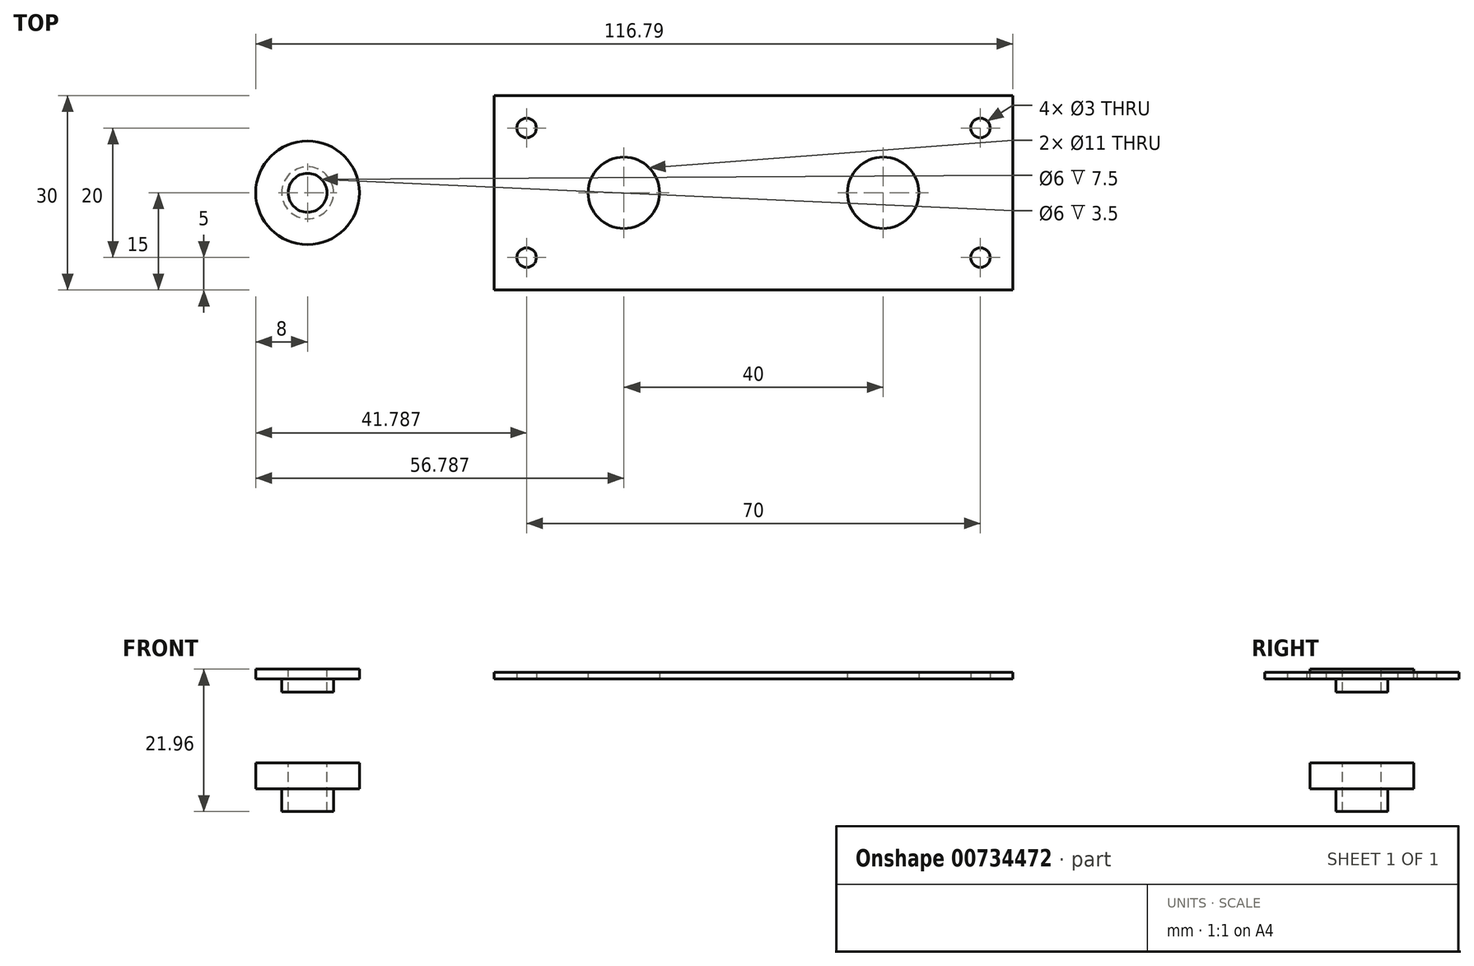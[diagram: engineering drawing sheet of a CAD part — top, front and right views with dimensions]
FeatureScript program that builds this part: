
annotation { "Feature Type Name" : "Feature", "Feature Type Description" : "" }
export const myFeature = defineFeature(function(context is Context, id is Id, definition is map)
    precondition{}
    {
        {
            var Q0;
            Q0=qCreatedBy(makeId("Front.planeOp"),FACE);
            var sketch = newSketch(context, id + "F0", { "sketchPlane" : qUnion([Q0])});
            skLineSegment(sketch, "E0", {"start": v(-3, 1.5) * mm, "end": v(-8, 1.5) * mm});
            skLineSegment(sketch, "E1", {"start": v(-8, 1.5) * mm, "end": v(-8, 0) * mm});
            skLineSegment(sketch, "E2", {"start": v(-8, 0) * mm, "end": v(-4, 0) * mm});
            skLineSegment(sketch, "E3", {"start": v(-4, 0) * mm, "end": v(-4, -2) * mm});
            skLineSegment(sketch, "E4", {"start": v(-4, -2) * mm, "end": v(-3, -2) * mm});
            skLineSegment(sketch, "E5", {"start": v(-3, -2) * mm, "end": v(-3, 1.5) * mm});
            skLineSegment(sketch, "E6", {"start": v(0, 13.9) * mm, "end": v(0, -9.75) * mm, "construction": true});
            skSolve(sketch);
        }
        {
            var Q0;
            Q0 = qSketchRegion(id + "F0", true);
            var Q1;
            Q1=sQuery(id+"F0.wireOp",EDGE,"E6");
            revolve(context, id + "F1", {"surfaceOperationType" : NewSurfaceOperationType.NEW, "entities" : qUnion([Q0]), "axis" : qUnion([Q1]), "revolveType" : RevolveType.FULL});
        }
        {
            var Q0;
            Q0=qCreatedBy(makeId("Top.planeOp"),FACE);
            var sketch = newSketch(context, id + "F2", { "sketchPlane" : qUnion([Q0])});
            skLineSegment(sketch, "E7.bottom", {"start": v(28.79, 15) * mm, "end": v(108.79, 15) * mm});
            skLineSegment(sketch, "E7.top", {"start": v(28.79, -15) * mm, "end": v(108.79, -15) * mm});
            skLineSegment(sketch, "E7.left", {"start": v(28.79, 15) * mm, "end": v(28.79, -15) * mm});
            skLineSegment(sketch, "E7.right", {"start": v(108.79, 15) * mm, "end": v(108.79, -15) * mm});
            skLineSegment(sketch, "E8", {"start": v(68.79, 32.99) * mm, "end": v(68.79, -27.71) * mm, "construction": true});
            skLineSegment(sketch, "E9", {"start": v(25.97, 0) * mm, "end": v(115.92, 0) * mm, "construction": true});
            skPoint(sketch, "E9.endSnap0", {"position": v(108.79, 0) * mm});
            skCircle(sketch, "E10", {"center": v(33.79, 10) * mm, "radius": 1.5 * mm});
            skCircle(sketch, "E11.MirrorC", {"center": v(33.79, -10) * mm, "radius": 1.5 * mm});
            skLineSegment(sketch, "E12.MirrorCS", {"start": v(68.79, -32.99) * mm, "end": v(68.79, 27.71) * mm, "construction": true});
            skCircle(sketch, "E13.MirrorC", {"center": v(103.79, 10) * mm, "radius": 1.5 * mm});
            skCircle(sketch, "E14.MirrorC", {"center": v(103.79, -10) * mm, "radius": 1.5 * mm});
            skCircle(sketch, "E15", {"center": v(48.79, 0) * mm, "radius": 5.5 * mm});
            skCircle(sketch, "E16.MirrorC", {"center": v(88.79, 0) * mm, "radius": 5.5 * mm});
            skSolve(sketch);
        }
        {
            var Q0;
            Q0 = qSketchRegion(id + "F2", true);
            extrude(context, id + "F3", {"entities" : qUnion([Q0]), "depth" : 1 * mm, "offsetDistance" : 25 * mm});
        }
        {
            var Q0;
            Q0=qCreatedBy(makeId("Front.planeOp"),FACE);
            var sketch = newSketch(context, id + "F4", { "sketchPlane" : qUnion([Q0])});
            skLineSegment(sketch, "E17", {"start": v(-3, -12.96) * mm, "end": v(-3, -20.46) * mm});
            skLineSegment(sketch, "E18", {"start": v(-3, -20.46) * mm, "end": v(-4, -20.46) * mm});
            skLineSegment(sketch, "E19", {"start": v(-4, -20.46) * mm, "end": v(-4, -16.96) * mm});
            skLineSegment(sketch, "E20", {"start": v(-4, -16.96) * mm, "end": v(-8, -16.96) * mm});
            skLineSegment(sketch, "E21", {"start": v(-8, -16.96) * mm, "end": v(-8, -12.96) * mm});
            skLineSegment(sketch, "E22", {"start": v(-8, -12.96) * mm, "end": v(-3, -12.96) * mm});
            skLineSegment(sketch, "E23", {"start": v(0, -6.52) * mm, "end": v(0, -28.57) * mm, "construction": true});
            skSolve(sketch);
        }
        {
            var Q0;
            Q0 = qSketchRegion(id + "F4", true);
            var Q1;
            Q1=sQuery(id+"F4.wireOp",EDGE,"E23");
            revolve(context, id + "F5", {"surfaceOperationType" : NewSurfaceOperationType.NEW, "entities" : qUnion([Q0]), "axis" : qUnion([Q1]), "revolveType" : RevolveType.FULL});
        }
    });
